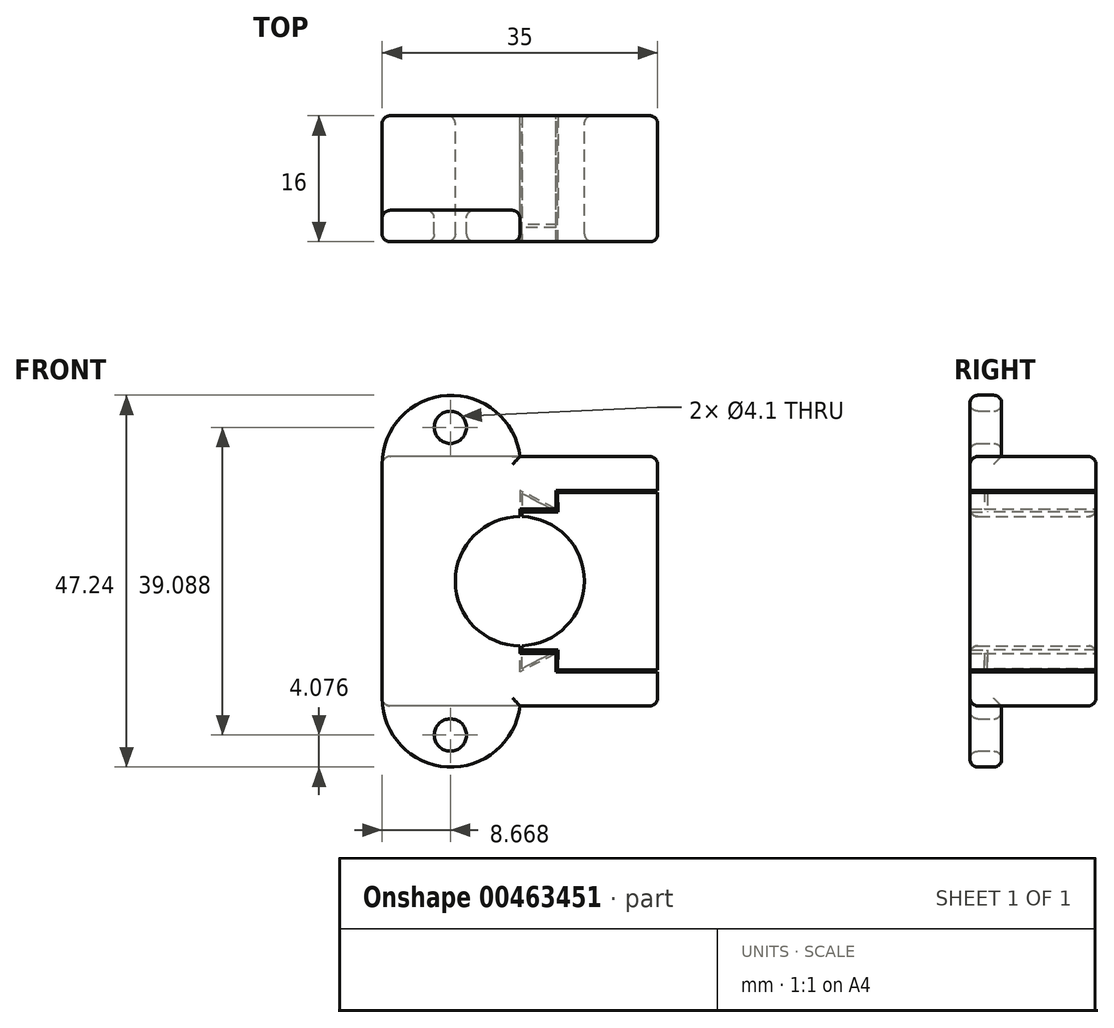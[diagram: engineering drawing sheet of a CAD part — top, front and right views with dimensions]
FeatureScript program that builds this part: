
annotation { "Feature Type Name" : "Feature", "Feature Type Description" : "" }
export const myFeature = defineFeature(function(context is Context, id is Id, definition is map)
    precondition{}
    {
        {
            var Q0;
            Q0=qCreatedBy(makeId("Front.planeOp"),FACE);
            var sketch = newSketch(context, id + "F0", { "sketchPlane" : qUnion([Q0])});
            skLineSegment(sketch, "E0.bottom", {"start": v(16.5, -15.84) * mm, "end": v(-16.5, -15.84) * mm});
            skLineSegment(sketch, "E0.top", {"start": v(16.5, 15.84) * mm, "end": v(5.5, 15.84) * mm});
            skLineSegment(sketch, "E0.left", {"start": v(17.5, -14.84) * mm, "end": v(17.5, -11.54) * mm});
            skLineSegment(sketch, "E0.right", {"start": v(-17.5, -14.84) * mm, "end": v(-17.5, 14.84) * mm});
            skPoint(sketch, "E1.middle", {"position": v(0, 0) * mm});
            skPoint(sketch, "E2.middle.positionSnap0", {"position": v(0, 15.84) * mm});
            skPoint(sketch, "E2.centerSnap0", {"position": v(0, 15.84) * mm});
            skLineSegment(sketch, "E3.trimOffspring", {"start": v(-5.5, 15.84) * mm, "end": v(-16.5, 15.84) * mm});
            skPoint(sketch, "E4.visualSharp", {"position": v(-17.5, 15.84) * mm});
            skArc(sketch, "E4.filletArc", {"start": v(-16.5, 15.84) * mm, "mid": v(-17.2, 15.55) * mm, "end": v(-17.5, 14.84) * mm});
            skPoint(sketch, "E5.visualSharp", {"position": v(17.5, 15.84) * mm});
            skArc(sketch, "E5.filletArc", {"start": v(17.5, 14.84) * mm, "mid": v(17.2, 15.55) * mm, "end": v(16.5, 15.84) * mm});
            skPoint(sketch, "E6.visualSharp", {"position": v(-17.5, -15.84) * mm});
            skArc(sketch, "E6.filletArc", {"start": v(-17.5, -14.84) * mm, "mid": v(-17.2, -15.55) * mm, "end": v(-16.5, -15.84) * mm});
            skPoint(sketch, "E7.visualSharp", {"position": v(17.5, -15.84) * mm});
            skArc(sketch, "E7.filletArc", {"start": v(16.5, -15.84) * mm, "mid": v(17.2, -15.55) * mm, "end": v(17.5, -14.84) * mm});
            skLineSegment(sketch, "E8.3", {"start": v(0, -11.54) * mm, "end": v(0, 0) * mm});
            skLineSegment(sketch, "E8.4", {"start": v(4.56, -9.17) * mm, "end": v(0, -11.54) * mm});
            skLineSegment(sketch, "E9.trimOffspring", {"start": v(17.5, -2.85) * mm, "end": v(17.5, 11.3) * mm});
            skLineSegment(sketch, "E10", {"start": v(4.56, -11.54) * mm, "end": v(17.5, -11.54) * mm});
            skCircle(sketch, "E11", {"center": v(0, 0) * mm, "radius": 8.2 * mm});
            skLineSegment(sketch, "E12.trimOffspring", {"start": v(17.5, 11.54) * mm, "end": v(17.5, 14.84) * mm});
            skLineSegment(sketch, "E13.trimOffspring", {"start": v(17.5, -11.3) * mm, "end": v(17.5, -2.85) * mm});
            skLineSegment(sketch, "E14", {"start": v(4.56, -9.17) * mm, "end": v(4.56, -11.54) * mm});
            skLineSegment(sketch, "E15.MirrorCS", {"start": v(0, 11.54) * mm, "end": v(0, 0) * mm});
            skLineSegment(sketch, "E16.MirrorCS", {"start": v(4.56, 9.17) * mm, "end": v(0, 11.54) * mm});
            skLineSegment(sketch, "E17.MirrorCS", {"start": v(4.56, 9.17) * mm, "end": v(4.56, 11.54) * mm});
            skLineSegment(sketch, "E18.MirrorCS", {"start": v(4.56, 11.54) * mm, "end": v(17.5, 11.54) * mm});
            skLineSegment(sketch, "E19.0", {"start": v(4.8, -11.3) * mm, "end": v(17.5, -11.3) * mm});
            skLineSegment(sketch, "E19.1", {"start": v(4.81, -8.76) * mm, "end": v(4.8, -11.3) * mm});
            skLineSegment(sketch, "E19.2", {"start": v(4.81, -8.76) * mm, "end": v(0.25, -11.13) * mm});
            skLineSegment(sketch, "E19.3", {"start": v(0.25, -11.13) * mm, "end": v(0.25, 0) * mm});
            skLineSegment(sketch, "E19.4", {"start": v(4.8, 11.3) * mm, "end": v(17.5, 11.3) * mm});
            skLineSegment(sketch, "E19.5", {"start": v(4.81, 8.76) * mm, "end": v(4.8, 11.3) * mm});
            skLineSegment(sketch, "E19.6", {"start": v(4.81, 8.76) * mm, "end": v(0.25, 11.13) * mm});
            skLineSegment(sketch, "E19.7", {"start": v(0.25, 11.13) * mm, "end": v(0.25, 0) * mm});
            skLineSegment(sketch, "E20", {"start": v(4.56, -9.17) * mm, "end": v(0, -9.16) * mm});
            skLineSegment(sketch, "E21", {"start": v(4.81, -8.76) * mm, "end": v(0.25, -8.75) * mm});
            skLineSegment(sketch, "E22", {"start": v(4.81, 8.76) * mm, "end": v(0.25, 8.76) * mm});
            skLineSegment(sketch, "E23", {"start": v(4.56, 9.17) * mm, "end": v(0, 9.17) * mm});
            skLineSegment(sketch, "E24", {"start": v(-5.5, 15.84) * mm, "end": v(5.5, 15.84) * mm});
            skLineSegment(sketch, "E25", {"start": v(0.25, 0) * mm, "end": v(37.04, 0) * mm, "construction": true});
            skLineSegment(sketch, "E26.1.0", {"start": v(3.55, -1.9) * mm, "end": v(-14.84, 29.96) * mm, "construction": true});
            skLineSegment(sketch, "E26.2.0", {"start": v(3.55, 1.9) * mm, "end": v(-14.84, -29.96) * mm, "construction": true});
            skPoint(sketch, "E26.center", {"position": v(2.45, 0) * mm});
            skArc(sketch, "E27", {"start": v(0, 15.84) * mm, "mid": v(-9.22, 23.6) * mm, "end": v(-17.5, 14.84) * mm});
            skArc(sketch, "E28.MirrorCS", {"start": v(0, -15.84) * mm, "mid": v(-9.22, -23.6) * mm, "end": v(-17.5, -14.84) * mm});
            skPoint(sketch, "E29", {"position": v(-8.83, 19.54) * mm});
            skPoint(sketch, "E30", {"position": v(-8.83, -19.54) * mm});
            skCircle(sketch, "E31", {"center": v(-8.83, 19.54) * mm, "radius": 2.05 * mm});
            skCircle(sketch, "E32.MirrorC", {"center": v(-8.83, -19.54) * mm, "radius": 2.05 * mm});
            skSolve(sketch);
        }
        {
            var Q0;
            Q0=makeQuery(id+"F0.imprint","IMPRINT",FACE,{"disambiguationData":[TD([[makeQuery(id+"F0.imprint","IMPRINT",EDGE,{"derivedFrom":sQuery(id+"F0.wireOp",EDGE,"E0.bottom")}),-1.0]])]});
            var Q1;
            {var subQ5=sQuery(id+"F0.wireOp",EDGE,"E9.trimOffspring");Q1=makeQuery(id+"F0.imprint","IMPRINT",FACE,{"disambiguationData":[TD([[makeQuery(id+"F0.imprint","IMPRINT",EDGE,{"derivedFrom":subQ5}),1.0]])]});}
            extrude(context, id + "F1", {"entities" : qUnion([Q0, Q1]), "depth" : 16 * mm, "offsetDistance" : 25 * mm, "symmetric" : true});
        }
        {
            var Q0;
            {var subQ1=sQuery(id+"F0.wireOp",EDGE,"E3.trimOffspring");Q0=makeQuery(id+"F0.imprint","IMPRINT",FACE,{"disambiguationData":[TD([[makeQuery(id+"F0.imprint","IMPRINT",EDGE,{"derivedFrom":subQ1}),-1.0]])]});}
            var Q1;
            {var subQ0=sQuery(id+"F0.wireOp",EDGE,"E6.filletArc");Q1=makeQuery(id+"F0.imprint","IMPRINT",FACE,{"disambiguationData":[TD([[makeQuery(id+"F0.imprint","IMPRINT",EDGE,{"derivedFrom":subQ0}),-1.0]])]});}
            extrude(context, id + "F2", {"entities" : qUnion([Q0, Q1]), "operationType" : NewBodyOperationType.ADD, "depth" : 8 * mm, "offsetDistance" : 25 * mm, "hasSecondDirection" : true, "secondDirectionOppositeDirection" : false, "secondDirectionDepth" : 4 * mm});
        }
        {
            var Q0;
            {var subQ8=sQuery(id+"F0.wireOp",EDGE,"E16.MirrorCS");Q0=makeQuery(id+"F0.imprint","IMPRINT",FACE,{"disambiguationData":[TD([[makeQuery(id+"F0.imprint","IMPRINT",EDGE,{"derivedFrom":subQ8}),1.0]])]});}
            var Q1;
            {var subQ0=sQuery(id+"F0.wireOp",EDGE,"E19.7");var subQ1=sQuery(id+"F0.wireOp",EDGE,"E19.6");var subQ2=makeQuery(id+"F0.imprint","INTERSECT",VERTEX,{"derivedFrom":[subQ1,subQ0]});Q1=makeQuery(id+"F0.imprint","IMPRINT",FACE,{"disambiguationData":[TD([[makeQuery(id+"F0.imprint","IMPRINT",EDGE,{"disambiguationData":[TD([[subQ2,1.0]])],"derivedFrom":subQ1}),1.0]])]});}
            var Q2;
            {var subQ0=sQuery(id+"F0.wireOp",EDGE,"E19.3");var subQ1=sQuery(id+"F0.wireOp",EDGE,"E19.2");var subQ2=makeQuery(id+"F0.imprint","INTERSECT",VERTEX,{"derivedFrom":[subQ1,subQ0]});Q2=makeQuery(id+"F0.imprint","IMPRINT",FACE,{"disambiguationData":[TD([[makeQuery(id+"F0.imprint","IMPRINT",EDGE,{"disambiguationData":[TD([[subQ2,1.0]])],"derivedFrom":subQ1}),-1.0]])]});}
            var Q3;
            {var subQ5=sQuery(id+"F0.wireOp",EDGE,"E8.4");Q3=makeQuery(id+"F0.imprint","IMPRINT",FACE,{"disambiguationData":[TD([[makeQuery(id+"F0.imprint","IMPRINT",EDGE,{"derivedFrom":subQ5}),-1.0]])]});}
            extrude(context, id + "F3", {"entities" : qUnion([Q0, Q1, Q2, Q3]), "operationType" : NewBodyOperationType.ADD, "depth" : 8 * mm, "hasSecondDirection" : true, "secondDirectionOppositeDirection" : false, "secondDirectionDepth" : 6.2 * mm, "offsetDistance" : 25 * mm});
        }
        {
            var Q0;
            {var subQ0=sQuery(id+"F0.wireOp",EDGE,"E22");Q0=makeQuery(id+"F0.imprint","IMPRINT",FACE,{"disambiguationData":[TD([[makeQuery(id+"F0.imprint","IMPRINT",EDGE,{"derivedFrom":subQ0}),-1.0]])]});}
            var Q1;
            {var subQ0=sQuery(id+"F0.wireOp",EDGE,"E19.7");var subQ1=sQuery(id+"F0.wireOp",EDGE,"E19.6");var subQ2=makeQuery(id+"F0.imprint","INTERSECT",VERTEX,{"derivedFrom":[subQ1,subQ0]});Q1=makeQuery(id+"F0.imprint","IMPRINT",FACE,{"disambiguationData":[TD([[makeQuery(id+"F0.imprint","IMPRINT",EDGE,{"disambiguationData":[TD([[subQ2,1.0]])],"derivedFrom":subQ1}),1.0]])]});}
            var Q2;
            {var subQ0=sQuery(id+"F0.wireOp",EDGE,"E21");Q2=makeQuery(id+"F0.imprint","IMPRINT",FACE,{"disambiguationData":[TD([[makeQuery(id+"F0.imprint","IMPRINT",EDGE,{"derivedFrom":subQ0}),1.0]])]});}
            var Q3;
            {var subQ0=sQuery(id+"F0.wireOp",EDGE,"E19.3");var subQ1=sQuery(id+"F0.wireOp",EDGE,"E19.2");var subQ2=makeQuery(id+"F0.imprint","INTERSECT",VERTEX,{"derivedFrom":[subQ1,subQ0]});Q3=makeQuery(id+"F0.imprint","IMPRINT",FACE,{"disambiguationData":[TD([[makeQuery(id+"F0.imprint","IMPRINT",EDGE,{"disambiguationData":[TD([[subQ2,1.0]])],"derivedFrom":subQ1}),-1.0]])]});}
            extrude(context, id + "F4", {"entities" : qUnion([Q0, Q1, Q2, Q3]), "operationType" : NewBodyOperationType.ADD, "depth" : -8 * mm, "hasSecondDirection" : true, "secondDirectionOppositeDirection" : false, "secondDirectionDepth" : 5.8 * mm, "offsetDistance" : 25 * mm});
        }
        {
            var Q0;
            Q0=makeQuery(id+"F1.opExtrude","CAP_EDGE",EDGE,{"disambiguationData":[OSD([sQuery(id+"F0.wireOp",EDGE,"E0.left")])],"isStart":false});
            var Q1;
            Q1=makeQuery(id+"F1.opExtrude","CAP_EDGE",EDGE,{"disambiguationData":[OSD([sQuery(id+"F0.wireOp",EDGE,"E9.trimOffspring"),sQuery(id+"F0.wireOp",EDGE,"E13.trimOffspring")])],"isStart":false});
            var Q2;
            Q2=makeQuery(id+"F1.opExtrude","CAP_EDGE",EDGE,{"disambiguationData":[OSD([sQuery(id+"F0.wireOp",EDGE,"E12.trimOffspring")])],"isStart":true});
            var Q3;
            Q3=makeQuery(id+"F1.opExtrude","CAP_EDGE",EDGE,{"disambiguationData":[OSD([sQuery(id+"F0.wireOp",EDGE,"E9.trimOffspring"),sQuery(id+"F0.wireOp",EDGE,"E13.trimOffspring")])],"isStart":true});
            var Q4;
            {var subQ0=sQuery(id+"F0.wireOp",EDGE,"E11");Q4=makeQuery(id+"F1.opExtrude","CAP_EDGE",EDGE,{"disambiguationData":[OSD([subQ0]),TDD([makeQuery(id+"F0.imprint","IMPRINT",EDGE,{"disambiguationData":[TD([[makeQuery(id+"F0.imprint","INTERSECT",VERTEX,{"derivedFrom":[subQ0,sQuery(id+"F0.wireOp",EDGE,"E19.7")]}),1.0]])],"derivedFrom":subQ0})])],"isStart":true});}
            var Q5;
            {var subQ0=sQuery(id+"F0.wireOp",EDGE,"E11");Q5=makeQuery(id+"F1.opExtrude","CAP_EDGE",EDGE,{"disambiguationData":[OSD([subQ0]),TDD([makeQuery(id+"F0.imprint","IMPRINT",EDGE,{"disambiguationData":[TD([[makeQuery(id+"F0.imprint","INTERSECT",VERTEX,{"derivedFrom":[sQuery(id+"F0.wireOp",EDGE,"E8.3"),subQ0]}),1.0]])],"derivedFrom":subQ0})])],"isStart":true});}
            var Q6;
            {var subQ0=sQuery(id+"F0.wireOp",EDGE,"E11");Q6=makeQuery(id+"F1.opExtrude","CAP_EDGE",EDGE,{"disambiguationData":[OSD([subQ0]),TDD([makeQuery(id+"F0.imprint","IMPRINT",EDGE,{"disambiguationData":[TD([[makeQuery(id+"F0.imprint","INTERSECT",VERTEX,{"derivedFrom":[subQ0,sQuery(id+"F0.wireOp",EDGE,"E19.7")]}),1.0]])],"derivedFrom":subQ0})])],"isStart":false});}
            var Q7;
            {var subQ0=sQuery(id+"F0.wireOp",EDGE,"E11");Q7=makeQuery(id+"F1.opExtrude","CAP_EDGE",EDGE,{"disambiguationData":[OSD([subQ0]),TDD([makeQuery(id+"F0.imprint","IMPRINT",EDGE,{"disambiguationData":[TD([[makeQuery(id+"F0.imprint","INTERSECT",VERTEX,{"derivedFrom":[sQuery(id+"F0.wireOp",EDGE,"E8.3"),subQ0]}),1.0]])],"derivedFrom":subQ0})])],"isStart":false});}
            var Q8;
            Q8=makeQuery(id+"F2.opExtrude","CAP_EDGE",EDGE,{"disambiguationData":[OSD([sQuery(id+"F0.wireOp",EDGE,"E28.MirrorCS")])],"isStart":false});
            var Q9;
            Q9=makeQuery(id+"F2.opExtrude","CAP_EDGE",EDGE,{"disambiguationData":[OSD([sQuery(id+"F0.wireOp",EDGE,"E28.MirrorCS")])],"isStart":true});
            var Q10;
            Q10=makeQuery(id+"F2.opExtrude","CAP_EDGE",EDGE,{"disambiguationData":[OSD([sQuery(id+"F0.wireOp",EDGE,"E27")])],"isStart":true});
            var Q11;
            Q11=makeQuery(id+"F1.opExtrude","CAP_EDGE",EDGE,{"disambiguationData":[OSD([sQuery(id+"F0.wireOp",EDGE,"E0.top"),sQuery(id+"F0.wireOp",EDGE,"E3.trimOffspring"),sQuery(id+"F0.wireOp",EDGE,"E24")])],"isStart":false});
            var Q12;
            Q12=makeQuery(id+"F2.opExtrude","CAP_EDGE",EDGE,{"disambiguationData":[OSD([sQuery(id+"F0.wireOp",EDGE,"E31")])],"isStart":true});
            var Q13;
            Q13=makeQuery(id+"F2.opExtrude","CAP_EDGE",EDGE,{"disambiguationData":[OSD([sQuery(id+"F0.wireOp",EDGE,"E32.MirrorC")])],"isStart":false});
            var Q14;
            Q14=makeQuery(id+"F2.opExtrude","CAP_EDGE",EDGE,{"disambiguationData":[OSD([sQuery(id+"F0.wireOp",EDGE,"E32.MirrorC")])],"isStart":true});
            var Q15;
            Q15=makeQuery(id+"F2.opExtrude","CAP_EDGE",EDGE,{"disambiguationData":[OSD([sQuery(id+"F0.wireOp",EDGE,"E31")])],"isStart":false});
            fillet(context, id + "F5", {"entities" : qUnion([Q0, Q1, Q2, Q3, Q4, Q5, Q6, Q7, Q8, Q9, Q10, Q11, Q12, Q13, Q14, Q15]), "radius" : 1 * mm, "tangentPropagation" : true, "allowEdgeOverflow" : false});
        }
    });
